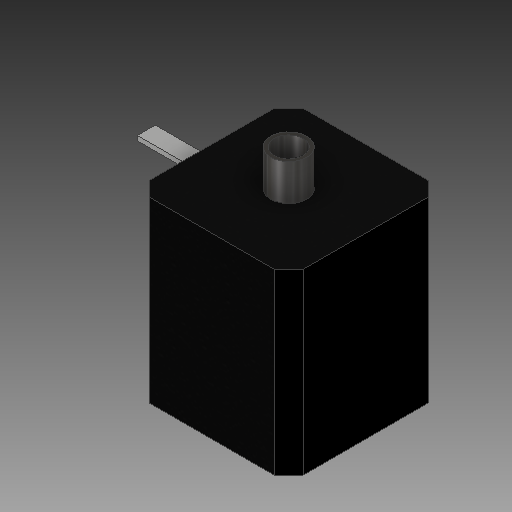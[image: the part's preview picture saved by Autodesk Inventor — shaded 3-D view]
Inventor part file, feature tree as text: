
AUTODESK INVENTOR PART (.ipt)
format: ipt  version: 2019 (Build 230136000, 136)  size: 174,080 bytes
history: native  units: in
note: dims shown in document units (in); Inventor stores cm internally (conversion verified against a paired STEP export)
features: extrude x5, sketch x4, chamfer x1, hole x1, projected_geometry x1
ambient origin geometry x8: Origin, YZ Plane, XZ Plane, XY Plane, X Axis, Y Axis, Z Axis, Center Point
bodies: Solid1 (feature_tree)
feature tree (12):
  sketch  "Sketch1"  dims[d0=1.6654in d1=1.9291in d2=0.0in]
  extrude  "Extrusion1"  Depth=1.9291in TaperAngle=0.0deg
  extrude  "Extrusion2"  Depth=0.7874in TaperAngle=0.0deg
  extrude  "Extrusion3"  Depth=0.0787in
  chamfer  "Chamfer1"  Distance=0.0787in
  extrude  "Extrusion4"  Depth=0.3937in
  extrude  "Extrusion5"  Depth=0.0787in
  hole  "Hole1"  [1 undecoded]
  sketch  "Sketch2"  dims[d3=0.0787in d4=0.0in d5=0.7874in d6=0.0in]
  sketch  "Sketch3"  dims[d7=0.1575in d8=0.0787in d9=45.0deg d10=0.2362in]
  projected_geometry  "Projected Loop1"
  sketch  "Sketch4"  dims[d11=0.8661in d12=0.0787in d13=0.0in d14=0.3937in d15=0.0394in d16=0.3937in d17=0.0in d18=1.2205in d19=0.0968in d20=0.2362in d21=0.1575in d22=0.0787in d23=90.0deg d24=0.3465in d25=0.8108in]
note: 1 required parameter value undecoded (feature->parameter linkage not recoverable at this tier; creation-order binding heuristic only, values carry confidence <= 0.55)
